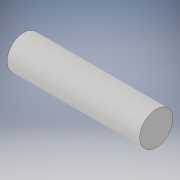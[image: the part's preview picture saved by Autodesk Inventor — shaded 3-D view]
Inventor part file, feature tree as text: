
AUTODESK INVENTOR PART (.ipt)
format: ipt  version: 2017 (Build 210142000, 142)  size: 96,256 bytes
history: native  units: in
note: dims shown in document units (in); Inventor stores cm internally (conversion verified against a paired STEP export)
features: extrude x1, sketch x1
ambient origin geometry x8: Origin, YZ Plane, XZ Plane, XY Plane, X Axis, Y Axis, Z Axis, Center Point
bodies: Solid1 (feature_tree)
feature tree (2):
  extrude  "Extrusion1"  Depth=0.5in TaperAngle=0.0deg
  sketch  "Sketch1"  dims[d0=0.125in d1=0.5in d2=0.0in]
